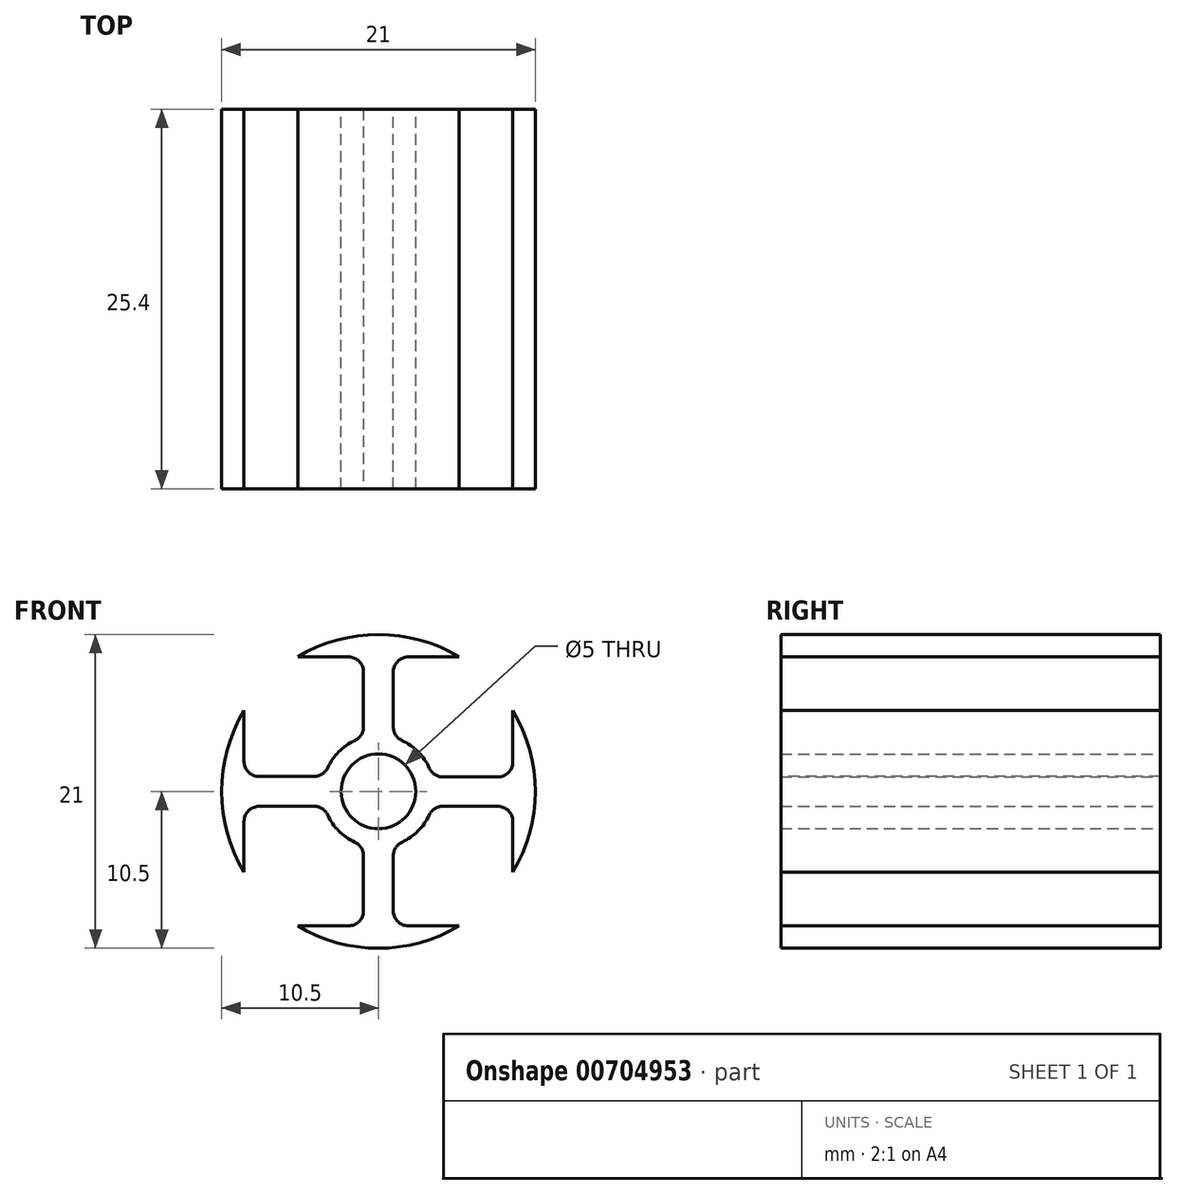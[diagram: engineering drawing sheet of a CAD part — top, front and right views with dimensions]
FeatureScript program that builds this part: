
annotation { "Feature Type Name" : "Feature", "Feature Type Description" : "" }
export const myFeature = defineFeature(function(context is Context, id is Id, definition is map)
    precondition{}
    {
        {
            var Q0;
            Q0=qCreatedBy(makeId("Front.planeOp"),FACE);
            var sketch = newSketch(context, id + "F0", { "sketchPlane" : qUnion([Q0])});
            skArc(sketch, "E0", {"start": v(-9, 5.4) * mm, "mid": v(-10.5, 0) * mm, "end": v(-9, -5.4) * mm});
            skLineSegment(sketch, "E1.bottom", {"start": v(5.4, 9) * mm, "end": v(-5.4, 9) * mm});
            skLineSegment(sketch, "E1.top", {"start": v(5.4, -9) * mm, "end": v(-5.4, -9) * mm});
            skLineSegment(sketch, "E1.left", {"start": v(9, 5.4) * mm, "end": v(9, -5.4) * mm});
            skLineSegment(sketch, "E1.right", {"start": v(-9, 5.4) * mm, "end": v(-9, -5.4) * mm});
            skLineSegment(sketch, "E2.bottom", {"start": v(-3.75, 0) * mm, "end": v(-9, 0) * mm});
            skLineSegment(sketch, "E2.right", {"start": v(-9, 0) * mm, "end": v(-9, 1) * mm});
            skLineSegment(sketch, "E3.right", {"start": v(-9, 0) * mm, "end": v(-9, -1) * mm});
            skLineSegment(sketch, "E4.bottom", {"start": v(3.75, 0) * mm, "end": v(9, 0) * mm});
            skLineSegment(sketch, "E4.right", {"start": v(9, 0) * mm, "end": v(9, 0.96) * mm});
            skLineSegment(sketch, "E5.right", {"start": v(9, 0) * mm, "end": v(9, -1) * mm});
            skLineSegment(sketch, "E6.top", {"start": v(0, 9) * mm, "end": v(1, 9) * mm});
            skLineSegment(sketch, "E7.top", {"start": v(0, 9) * mm, "end": v(-1, 9) * mm});
            skLineSegment(sketch, "E8.top", {"start": v(0, -9) * mm, "end": v(1, -9) * mm});
            skLineSegment(sketch, "E9.top", {"start": v(0, -9) * mm, "end": v(-1, -9) * mm});
            skLineSegment(sketch, "E9.right", {"start": v(-1, -3.61) * mm, "end": v(-1, -9) * mm});
            skPoint(sketch, "E10", {"position": v(-5.4, 9) * mm});
            skPoint(sketch, "E11", {"position": v(-9, 5.4) * mm});
            skPoint(sketch, "E12", {"position": v(-9, 9) * mm});
            skArc(sketch, "E13.trimOffspring", {"start": v(-5.4, -9) * mm, "mid": v(0, -10.5) * mm, "end": v(5.4, -9) * mm});
            skPoint(sketch, "E14.orphan", {"position": v(-9, -9) * mm});
            skPoint(sketch, "E15.orphan", {"position": v(9, -9) * mm});
            skArc(sketch, "E16.trimOffspring", {"start": v(9, -5.4) * mm, "mid": v(10.5, 0) * mm, "end": v(9, 5.4) * mm});
            skArc(sketch, "E17.trimOffspring", {"start": v(5.4, 9) * mm, "mid": v(0, 10.5) * mm, "end": v(-5.4, 9) * mm});
            skPoint(sketch, "E18.orphan", {"position": v(9, 9) * mm});
            skLineSegment(sketch, "E19.trimOffspring", {"start": v(3.62, 0.96) * mm, "end": v(9, 0.96) * mm});
            skLineSegment(sketch, "E20.trimOffspring", {"start": v(1, 3.61) * mm, "end": v(1, 9) * mm});
            skLineSegment(sketch, "E21.trimOffspring", {"start": v(0, 3.75) * mm, "end": v(0, 9) * mm});
            skLineSegment(sketch, "E22.trimOffspring", {"start": v(-1, 3.61) * mm, "end": v(-1, 9) * mm});
            skLineSegment(sketch, "E23.trimOffspring", {"start": v(-3.61, 1) * mm, "end": v(-9, 1) * mm});
            skLineSegment(sketch, "E24.trimOffspring", {"start": v(-3.61, -1) * mm, "end": v(-9, -1) * mm});
            skLineSegment(sketch, "E25.trimOffspring", {"start": v(3.61, -1) * mm, "end": v(9, -1) * mm});
            skCircle(sketch, "E26", {"center": v(0, 0) * mm, "radius": 3.75 * mm});
            skLineSegment(sketch, "E27.trimOffspring", {"start": v(1, -3.61) * mm, "end": v(1, -9) * mm});
            skLineSegment(sketch, "E28.trimOffspring", {"start": v(0, -3.75) * mm, "end": v(0, -9) * mm});
            skCircle(sketch, "E29", {"center": v(0, 0) * mm, "radius": 2.5 * mm});
            skPoint(sketch, "E30", {"position": v(0, 2.5) * mm});
            skPoint(sketch, "E31", {"position": v(2.5, 0) * mm});
            skPoint(sketch, "E32", {"position": v(0, -2.5) * mm});
            skPoint(sketch, "E33", {"position": v(-2.5, 0) * mm});
            skLineSegment(sketch, "E34", {"start": v(0, 0) * mm, "end": v(-2.5, 0) * mm});
            skLineSegment(sketch, "E35", {"start": v(0, 0) * mm, "end": v(0, 2.5) * mm});
            skLineSegment(sketch, "E36", {"start": v(0, 0) * mm, "end": v(2.5, 0) * mm});
            skLineSegment(sketch, "E37", {"start": v(0, 0) * mm, "end": v(0, -2.5) * mm});
            skSolve(sketch);
        }
        {
            var Q0;
            Q0=qSketchRegion(id+"F0",true);
            extrude(context, id + "F1", {"entities" : qUnion([Q0]), "depth" : 25.4 * mm, "offsetDistance" : 25.4 * mm});
        }
        {
            var Q0;
            Q0=makeQuery(id+"F1.opExtrude","SWEPT_EDGE",EDGE,{"disambiguationData":[OSD([sQuery(id+"F0.wireOp",EDGE,"E24.trimOffspring"),sQuery(id+"F0.wireOp",EDGE,"E26")])]});
            var Q1;
            Q1=makeQuery(id+"F1.opExtrude","SWEPT_EDGE",EDGE,{"disambiguationData":[OSD([sQuery(id+"F0.wireOp",EDGE,"E1.right"),sQuery(id+"F0.wireOp",EDGE,"E3.right"),sQuery(id+"F0.wireOp",EDGE,"E24.trimOffspring")])]});
            var Q2;
            Q2=makeQuery(id+"F1.opExtrude","SWEPT_EDGE",EDGE,{"disambiguationData":[OSD([sQuery(id+"F0.wireOp",EDGE,"E1.right"),sQuery(id+"F0.wireOp",EDGE,"E2.right"),sQuery(id+"F0.wireOp",EDGE,"E23.trimOffspring")])]});
            var Q3;
            Q3=makeQuery(id+"F1.opExtrude","SWEPT_EDGE",EDGE,{"disambiguationData":[OSD([sQuery(id+"F0.wireOp",EDGE,"E19.trimOffspring"),sQuery(id+"F0.wireOp",EDGE,"E26")])]});
            var Q4;
            Q4=makeQuery(id+"F1.opExtrude","SWEPT_EDGE",EDGE,{"disambiguationData":[OSD([sQuery(id+"F0.wireOp",EDGE,"E20.trimOffspring"),sQuery(id+"F0.wireOp",EDGE,"E26")])]});
            var Q5;
            Q5=makeQuery(id+"F1.opExtrude","SWEPT_EDGE",EDGE,{"disambiguationData":[OSD([sQuery(id+"F0.wireOp",EDGE,"E26"),sQuery(id+"F0.wireOp",EDGE,"E27.trimOffspring")])]});
            var Q6;
            Q6=makeQuery(id+"F1.opExtrude","SWEPT_EDGE",EDGE,{"disambiguationData":[OSD([sQuery(id+"F0.wireOp",EDGE,"E25.trimOffspring"),sQuery(id+"F0.wireOp",EDGE,"E26")])]});
            var Q7;
            Q7=makeQuery(id+"F1.opExtrude","SWEPT_EDGE",EDGE,{"disambiguationData":[OSD([sQuery(id+"F0.wireOp",EDGE,"E1.top"),sQuery(id+"F0.wireOp",EDGE,"E8.top"),sQuery(id+"F0.wireOp",EDGE,"E27.trimOffspring")])]});
            var Q8;
            Q8=makeQuery(id+"F1.opExtrude","SWEPT_EDGE",EDGE,{"disambiguationData":[OSD([sQuery(id+"F0.wireOp",EDGE,"E1.top"),sQuery(id+"F0.wireOp",EDGE,"E9.top"),sQuery(id+"F0.wireOp",EDGE,"E9.right")])]});
            var Q9;
            Q9=makeQuery(id+"F1.opExtrude","SWEPT_EDGE",EDGE,{"disambiguationData":[OSD([sQuery(id+"F0.wireOp",EDGE,"E1.bottom"),sQuery(id+"F0.wireOp",EDGE,"E7.top"),sQuery(id+"F0.wireOp",EDGE,"E22.trimOffspring")])]});
            var Q10;
            Q10=makeQuery(id+"F1.opExtrude","SWEPT_EDGE",EDGE,{"disambiguationData":[OSD([sQuery(id+"F0.wireOp",EDGE,"E1.bottom"),sQuery(id+"F0.wireOp",EDGE,"E6.top"),sQuery(id+"F0.wireOp",EDGE,"E20.trimOffspring")])]});
            var Q11;
            Q11=makeQuery(id+"F1.opExtrude","SWEPT_EDGE",EDGE,{"disambiguationData":[OSD([sQuery(id+"F0.wireOp",EDGE,"E1.left"),sQuery(id+"F0.wireOp",EDGE,"E5.right"),sQuery(id+"F0.wireOp",EDGE,"E25.trimOffspring")])]});
            var Q12;
            Q12=makeQuery(id+"F1.opExtrude","SWEPT_EDGE",EDGE,{"disambiguationData":[OSD([sQuery(id+"F0.wireOp",EDGE,"E1.left"),sQuery(id+"F0.wireOp",EDGE,"E4.right"),sQuery(id+"F0.wireOp",EDGE,"E19.trimOffspring")])]});
            var Q13;
            Q13=makeQuery(id+"F1.opExtrude","SWEPT_EDGE",EDGE,{"disambiguationData":[OSD([sQuery(id+"F0.wireOp",EDGE,"E22.trimOffspring"),sQuery(id+"F0.wireOp",EDGE,"E26")])]});
            var Q14;
            Q14=makeQuery(id+"F1.opExtrude","SWEPT_EDGE",EDGE,{"disambiguationData":[OSD([sQuery(id+"F0.wireOp",EDGE,"E23.trimOffspring"),sQuery(id+"F0.wireOp",EDGE,"E26")])]});
            var Q15;
            Q15=makeQuery(id+"F1.opExtrude","SWEPT_EDGE",EDGE,{"disambiguationData":[OSD([sQuery(id+"F0.wireOp",EDGE,"E9.right"),sQuery(id+"F0.wireOp",EDGE,"E26")])]});
            fillet(context, id + "F2", {"entities" : qUnion([Q0, Q1, Q2, Q3, Q4, Q5, Q6, Q7, Q8, Q9, Q10, Q11, Q12, Q13, Q14, Q15]), "radius" : 1 * mm, "tangentPropagation" : true, "allowEdgeOverflow" : false});
        }
    });
